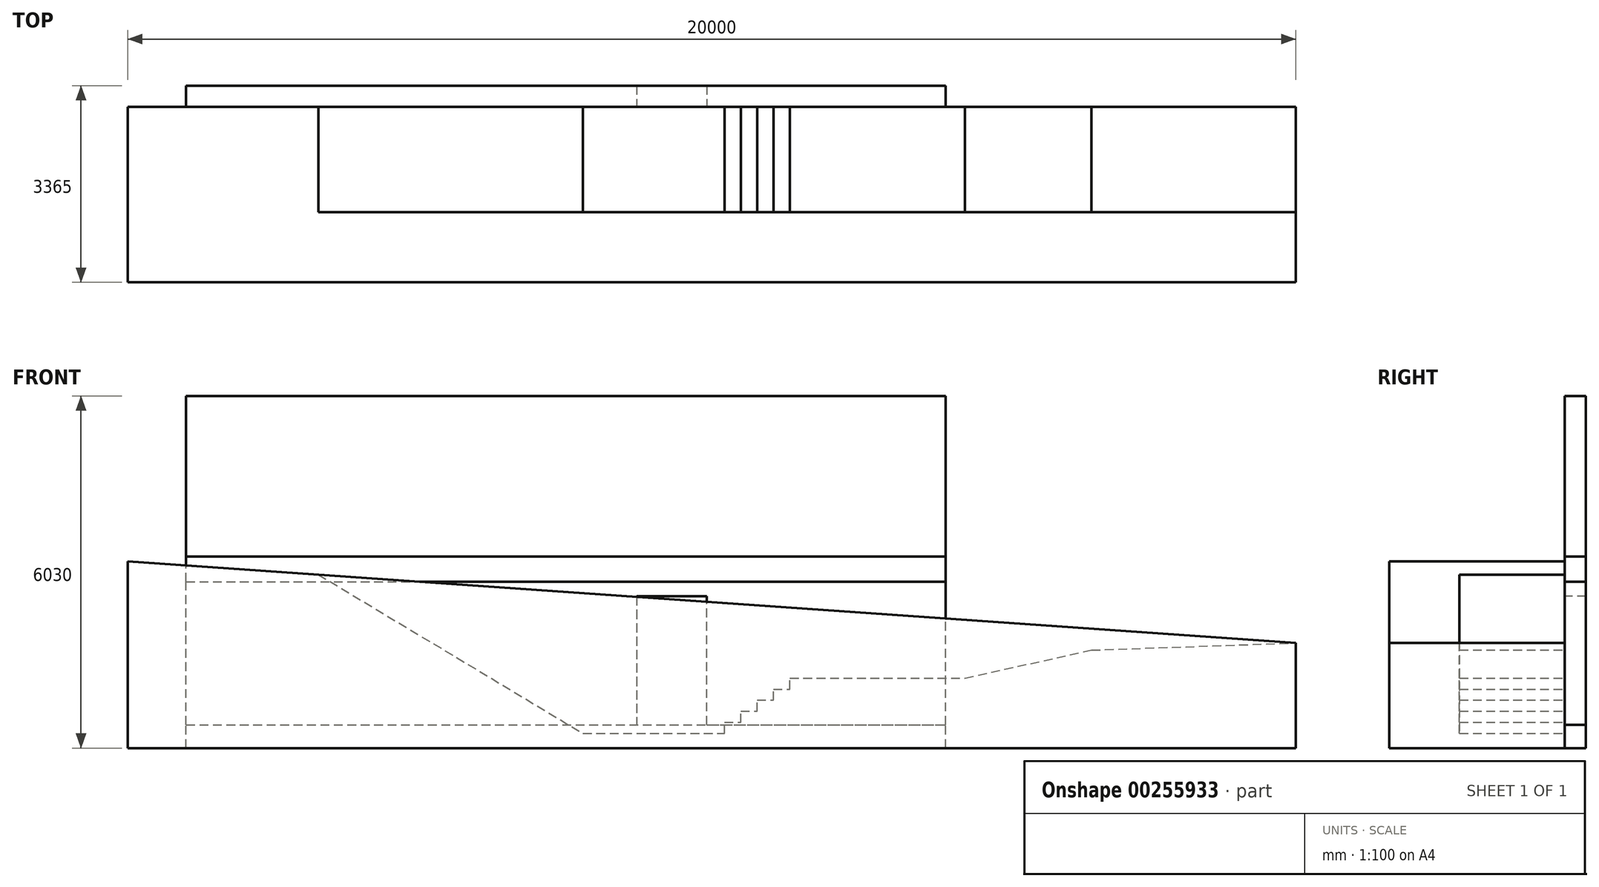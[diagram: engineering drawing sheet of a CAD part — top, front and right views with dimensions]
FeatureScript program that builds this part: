
annotation { "Feature Type Name" : "Feature", "Feature Type Description" : "" }
export const myFeature = defineFeature(function(context is Context, id is Id, definition is map)
    precondition{}
    {
        {
            var Q0;
            Q0=qCreatedBy(makeId("Front.planeOp"),FACE);
            var sketch = newSketch(context, id + "F0", { "sketchPlane" : qUnion([Q0])});
            skLineSegment(sketch, "E0.bottom", {"start": v(0, 0) * mm, "end": v(13000, 0) * mm});
            skLineSegment(sketch, "E0.top", {"start": v(0, 400) * mm, "end": v(13000, 400) * mm});
            skLineSegment(sketch, "E0.left", {"start": v(0, 0) * mm, "end": v(0, 400) * mm});
            skLineSegment(sketch, "E0.right", {"start": v(13000, 0) * mm, "end": v(13000, 400) * mm});
            skSolve(sketch);
        }
        {
            var Q0;
            Q0=qSketchRegion(id+"F0",true);
            extrude(context, id + "F1", {"entities" : qUnion([Q0]), "depth" : 365 * mm});
        }
        {
            var Q0;
            Q0=makeQuery(id+"F1.opExtrude","CAP_FACE",FACE,{"disambiguationData":[OSD([sQuery(id+"F0.wireOp",EDGE,"E0.bottom"),sQuery(id+"F0.wireOp",EDGE,"E0.top"),sQuery(id+"F0.wireOp",EDGE,"E0.left"),sQuery(id+"F0.wireOp",EDGE,"E0.right")])],"isStart":false});
            var sketch = newSketch(context, id + "F2", { "sketchPlane" : qUnion([Q0])});
            skLineSegment(sketch, "E1.bottom", {"start": v(0, 400) * mm, "end": v(7715, 400) * mm});
            skLineSegment(sketch, "E1.top", {"start": v(0, 2850) * mm, "end": v(13000, 2850) * mm});
            skLineSegment(sketch, "E1.left", {"start": v(0, 400) * mm, "end": v(0, 2850) * mm});
            skLineSegment(sketch, "E1.right", {"start": v(13000, 400) * mm, "end": v(13000, 2850) * mm});
            skLineSegment(sketch, "E2", {"start": v(8915, 400) * mm, "end": v(8915, 2600) * mm});
            skLineSegment(sketch, "E3", {"start": v(8915, 2600) * mm, "end": v(7715, 2600) * mm});
            skLineSegment(sketch, "E4", {"start": v(7715, 2600) * mm, "end": v(7715, 400) * mm});
            skLineSegment(sketch, "E5.trimOffspring", {"start": v(8915, 400) * mm, "end": v(13000, 400) * mm});
            skSolve(sketch);
        }
        {
            var Q0;
            Q0=qSketchRegion(id+"F2",true);
            extrude(context, id + "F3", {"entities" : qUnion([Q0]), "oppositeDirection" : true, "depth" : 365 * mm});
        }
        {
            var Q0;
            Q0=qCreatedBy(makeId("Front.planeOp"),FACE);
            var sketch = newSketch(context, id + "F4", { "sketchPlane" : qUnion([Q0])});
            skLineSegment(sketch, "E6.bottom", {"start": v(0, 2850) * mm, "end": v(13000, 2850) * mm});
            skLineSegment(sketch, "E6.top", {"start": v(0, 3280) * mm, "end": v(13000, 3280) * mm});
            skLineSegment(sketch, "E6.left", {"start": v(0, 2850) * mm, "end": v(0, 3280) * mm});
            skLineSegment(sketch, "E6.right", {"start": v(13000, 2850) * mm, "end": v(13000, 3280) * mm});
            skSolve(sketch);
        }
        {
            var Q0;
            Q0=qSketchRegion(id+"F4",true);
            extrude(context, id + "F5", {"entities" : qUnion([Q0]), "depth" : 365 * mm});
        }
        {
            var Q0;
            Q0=qCreatedBy(makeId("Front.planeOp"),FACE);
            var sketch = newSketch(context, id + "F6", { "sketchPlane" : qUnion([Q0])});
            skLineSegment(sketch, "E7.bottom", {"start": v(0, 3280) * mm, "end": v(13000, 3280) * mm});
            skLineSegment(sketch, "E7.top", {"start": v(0, 6030) * mm, "end": v(13000, 6030) * mm});
            skLineSegment(sketch, "E7.left", {"start": v(0, 3280) * mm, "end": v(0, 6030) * mm});
            skLineSegment(sketch, "E7.right", {"start": v(13000, 3280) * mm, "end": v(13000, 6030) * mm});
            skSolve(sketch);
        }
        {
            var Q0;
            Q0=qSketchRegion(id+"F6",true);
            extrude(context, id + "F7", {"entities" : qUnion([Q0]), "depth" : 365 * mm});
        }
        {
            var Q0;
            Q0=makeQuery(id+"F3.opExtrude","CAP_FACE",FACE,{"disambiguationData":[OSD([sQuery(id+"F2.wireOp",EDGE,"E1.bottom"),sQuery(id+"F2.wireOp",EDGE,"E1.top"),sQuery(id+"F2.wireOp",EDGE,"E1.left"),sQuery(id+"F2.wireOp",EDGE,"E1.right"),sQuery(id+"F2.wireOp",EDGE,"E2"),sQuery(id+"F2.wireOp",EDGE,"E3"),sQuery(id+"F2.wireOp",EDGE,"E4"),sQuery(id+"F2.wireOp",EDGE,"E5.trimOffspring")])],"isStart":true});
            var sketch = newSketch(context, id + "F8", { "sketchPlane" : qUnion([Q0])});
            skLineSegment(sketch, "E8", {"start": v(-1000, 3200) * mm, "end": v(19000, 1800) * mm});
            skLineSegment(sketch, "E9", {"start": v(19000, 1800) * mm, "end": v(19000, 0) * mm});
            skLineSegment(sketch, "E10", {"start": v(19000, 0) * mm, "end": v(-1000, 0) * mm});
            skLineSegment(sketch, "E11", {"start": v(-1000, 3200) * mm, "end": v(-1000, 0) * mm});
            skPoint(sketch, "E12", {"position": v(0, 3130) * mm});
            skSolve(sketch);
        }
        {
            var Q0;
            Q0=qSketchRegion(id+"F8",true);
            extrude(context, id + "F9", {"entities" : qUnion([Q0]), "depth" : 3000 * mm});
        }
        {
            var Q0;
            Q0=makeQuery(id+"F3.opExtrude","CAP_FACE",FACE,{"disambiguationData":[OSD([sQuery(id+"F2.wireOp",EDGE,"E1.bottom"),sQuery(id+"F2.wireOp",EDGE,"E1.top"),sQuery(id+"F2.wireOp",EDGE,"E1.left"),sQuery(id+"F2.wireOp",EDGE,"E1.right"),sQuery(id+"F2.wireOp",EDGE,"E2"),sQuery(id+"F2.wireOp",EDGE,"E3"),sQuery(id+"F2.wireOp",EDGE,"E4"),sQuery(id+"F2.wireOp",EDGE,"E5.trimOffspring")])],"isStart":true});
            var sketch = newSketch(context, id + "F10", { "sketchPlane" : qUnion([Q0])});
            skLineSegment(sketch, "E13", {"start": v(2000, 3130) * mm, "end": v(6793.12, 250) * mm});
            skLineSegment(sketch, "E14", {"start": v(6793.12, 250) * mm, "end": v(9215, 250) * mm});
            skLineSegment(sketch, "E15", {"start": v(15500, 1677.78) * mm, "end": v(19000, 1800) * mm});
            skLineSegment(sketch, "E16", {"start": v(19000, 1800) * mm, "end": v(19000, 0) * mm});
            skLineSegment(sketch, "E17", {"start": v(0, 0) * mm, "end": v(0, 3130) * mm});
            skLineSegment(sketch, "E18", {"start": v(9215, 250) * mm, "end": v(9215, 440) * mm});
            skLineSegment(sketch, "E19", {"start": v(9215, 440) * mm, "end": v(9495, 440) * mm});
            skLineSegment(sketch, "E20", {"start": v(9495, 440) * mm, "end": v(9495, 630) * mm});
            skLineSegment(sketch, "E21", {"start": v(9495, 630) * mm, "end": v(9775, 630) * mm});
            skLineSegment(sketch, "E22", {"start": v(9775, 630) * mm, "end": v(9775, 820) * mm});
            skLineSegment(sketch, "E23", {"start": v(9775, 820) * mm, "end": v(10055, 820) * mm});
            skLineSegment(sketch, "E24", {"start": v(10055, 820) * mm, "end": v(10055, 1010) * mm});
            skPoint(sketch, "E25", {"position": v(11027.37, 2300) * mm});
            skLineSegment(sketch, "E26", {"start": v(10055, 1010) * mm, "end": v(10335, 1010) * mm});
            skLineSegment(sketch, "E27", {"start": v(10335, 1010) * mm, "end": v(10335, 1200) * mm});
            skLineSegment(sketch, "E28", {"start": v(10335, 1200) * mm, "end": v(13335, 1200) * mm});
            skLineSegment(sketch, "E29", {"start": v(13335, 1200) * mm, "end": v(15500, 1677.78) * mm});
            skLineSegment(sketch, "E30", {"start": v(2000, 3130) * mm, "end": v(19000, 3130) * mm});
            skLineSegment(sketch, "E31", {"start": v(19000, 3130) * mm, "end": v(19000, 1800) * mm});
            skSolve(sketch);
        }
        {
            var Q0;
            Q0=qSketchRegion(id+"F10",true);
            extrude(context, id + "F11", {"entities" : qUnion([Q0]), "operationType" : NewBodyOperationType.REMOVE, "depth" : 1800 * mm});
        }
    });
